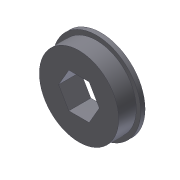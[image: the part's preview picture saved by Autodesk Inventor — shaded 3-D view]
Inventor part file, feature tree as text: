
AUTODESK INVENTOR PART (.ipt)
format: ipt  version: 2012 (Build 160160000, 160)  size: 93,184 bytes
history: native  units: in
note: dims shown in document units (in); Inventor stores cm internally (conversion verified against a paired STEP export)
features: extrude x2, sketch x2
ambient origin geometry x8: Origin, YZ Plane, XZ Plane, XY Plane, X Axis, Y Axis, Z Axis, Center Point
bodies: Solid1 (feature_tree)
feature tree (4):
  extrude  "Extrusion1"  Depth=0.5in
  extrude  "Extrusion2"  Depth=0.0625in
  sketch  "Sketch1"  dims[d0=1.25in d1=0.5in]
  sketch  "Sketch2"  dims[d2=0.312in d3=0.0in d4=0.0625in d5=0.2495in d6=0.0in]
